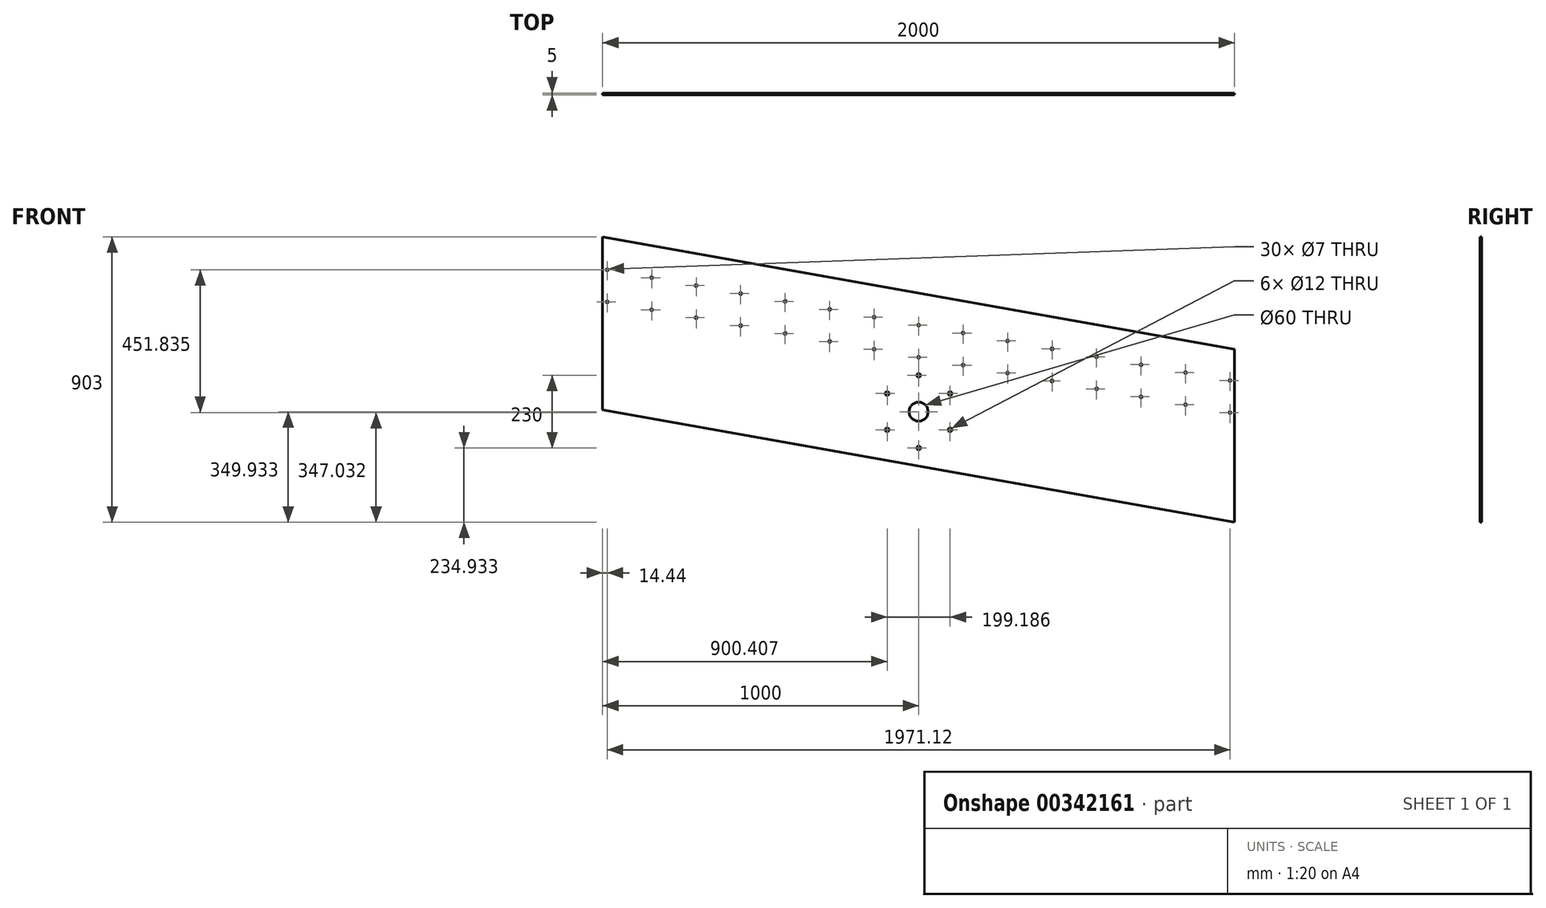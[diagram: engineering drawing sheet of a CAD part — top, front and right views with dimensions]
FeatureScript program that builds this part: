
annotation { "Feature Type Name" : "Feature", "Feature Type Description" : "" }
export const myFeature = defineFeature(function(context is Context, id is Id, definition is map)
    precondition{}
    {
        {
            var Q0;
            Q0=qCreatedBy(makeId("Front.planeOp"),FACE);
            var sketch = newSketch(context, id + "F0", { "sketchPlane" : qUnion([Q0])});
            skLineSegment(sketch, "E0", {"start": v(1435, 0) * mm, "end": v(1435, 547.6) * mm});
            skLineSegment(sketch, "E1", {"start": v(1435, 547.6) * mm, "end": v(-565, 903) * mm});
            skLineSegment(sketch, "E2", {"start": v(-565, 903) * mm, "end": v(-565, 355.4) * mm});
            skLineSegment(sketch, "E3", {"start": v(1435, 344.47) * mm, "end": v(1420.56, 347.03) * mm, "construction": true});
            skCircle(sketch, "E4", {"center": v(-550.56, 798.87) * mm, "radius": 3.5 * mm});
            skCircle(sketch, "E5", {"center": v(-550.56, 697.3) * mm, "radius": 3.5 * mm});
            skLineSegment(sketch, "E6.1.0.0", {"start": v(-409.77, 773.85) * mm, "end": v(-409.77, 672.28) * mm, "construction": true});
            skCircle(sketch, "E6.1.0.1", {"center": v(-409.77, 773.85) * mm, "radius": 3.5 * mm});
            skCircle(sketch, "E6.1.0.2", {"center": v(-409.77, 672.28) * mm, "radius": 3.5 * mm});
            skLineSegment(sketch, "E6.2.0.0", {"start": v(-268.97, 748.83) * mm, "end": v(-268.97, 647.26) * mm, "construction": true});
            skCircle(sketch, "E6.2.0.1", {"center": v(-268.97, 748.83) * mm, "radius": 3.5 * mm});
            skCircle(sketch, "E6.2.0.2", {"center": v(-268.97, 647.26) * mm, "radius": 3.5 * mm});
            skLineSegment(sketch, "E6.3.0.0", {"start": v(-128.18, 723.8) * mm, "end": v(-128.18, 622.24) * mm, "construction": true});
            skCircle(sketch, "E6.3.0.1", {"center": v(-128.18, 723.8) * mm, "radius": 3.5 * mm});
            skCircle(sketch, "E6.3.0.2", {"center": v(-128.18, 622.24) * mm, "radius": 3.5 * mm});
            skLineSegment(sketch, "E6.4.0.0", {"start": v(12.62, 698.8) * mm, "end": v(12.62, 597.22) * mm, "construction": true});
            skCircle(sketch, "E6.4.0.1", {"center": v(12.62, 698.8) * mm, "radius": 3.5 * mm});
            skCircle(sketch, "E6.4.0.2", {"center": v(12.62, 597.22) * mm, "radius": 3.5 * mm});
            skLineSegment(sketch, "E6.5.0.0", {"start": v(153.41, 673.77) * mm, "end": v(153.41, 572.2) * mm, "construction": true});
            skCircle(sketch, "E6.5.0.1", {"center": v(153.41, 673.77) * mm, "radius": 3.5 * mm});
            skCircle(sketch, "E6.5.0.2", {"center": v(153.41, 572.2) * mm, "radius": 3.5 * mm});
            skLineSegment(sketch, "E6.6.0.0", {"start": v(294.2, 648.75) * mm, "end": v(294.2, 547.19) * mm, "construction": true});
            skCircle(sketch, "E6.6.0.1", {"center": v(294.2, 648.75) * mm, "radius": 3.5 * mm});
            skCircle(sketch, "E6.6.0.2", {"center": v(294.2, 547.19) * mm, "radius": 3.5 * mm});
            skLineSegment(sketch, "E6.7.0.0", {"start": v(435, 623.73) * mm, "end": v(435, 522.17) * mm, "construction": true});
            skCircle(sketch, "E6.7.0.1", {"center": v(435, 623.73) * mm, "radius": 3.5 * mm});
            skCircle(sketch, "E6.7.0.2", {"center": v(435, 522.17) * mm, "radius": 3.5 * mm});
            skLineSegment(sketch, "E6.8.0.0", {"start": v(575.8, 598.71) * mm, "end": v(575.8, 497.15) * mm, "construction": true});
            skCircle(sketch, "E6.8.0.1", {"center": v(575.8, 598.71) * mm, "radius": 3.5 * mm});
            skCircle(sketch, "E6.8.0.2", {"center": v(575.8, 497.15) * mm, "radius": 3.5 * mm});
            skLineSegment(sketch, "E6.9.0.0", {"start": v(716.59, 573.7) * mm, "end": v(716.59, 472.13) * mm, "construction": true});
            skCircle(sketch, "E6.9.0.1", {"center": v(716.59, 573.7) * mm, "radius": 3.5 * mm});
            skCircle(sketch, "E6.9.0.2", {"center": v(716.59, 472.13) * mm, "radius": 3.5 * mm});
            skLineSegment(sketch, "E6.10.0.0", {"start": v(857.38, 548.68) * mm, "end": v(857.38, 447.1) * mm, "construction": true});
            skCircle(sketch, "E6.10.0.1", {"center": v(857.38, 548.68) * mm, "radius": 3.5 * mm});
            skCircle(sketch, "E6.10.0.2", {"center": v(857.38, 447.1) * mm, "radius": 3.5 * mm});
            skLineSegment(sketch, "E6.11.0.0", {"start": v(998.18, 523.66) * mm, "end": v(998.18, 422.09) * mm, "construction": true});
            skCircle(sketch, "E6.11.0.1", {"center": v(998.18, 523.66) * mm, "radius": 3.5 * mm});
            skCircle(sketch, "E6.11.0.2", {"center": v(998.18, 422.09) * mm, "radius": 3.5 * mm});
            skLineSegment(sketch, "E6.12.0.0", {"start": v(1138.97, 498.64) * mm, "end": v(1138.97, 397.07) * mm, "construction": true});
            skCircle(sketch, "E6.12.0.1", {"center": v(1138.97, 498.64) * mm, "radius": 3.5 * mm});
            skCircle(sketch, "E6.12.0.2", {"center": v(1138.97, 397.07) * mm, "radius": 3.5 * mm});
            skLineSegment(sketch, "E6.13.0.0", {"start": v(1279.77, 473.62) * mm, "end": v(1279.77, 372.05) * mm, "construction": true});
            skCircle(sketch, "E6.13.0.1", {"center": v(1279.77, 473.62) * mm, "radius": 3.5 * mm});
            skCircle(sketch, "E6.13.0.2", {"center": v(1279.77, 372.05) * mm, "radius": 3.5 * mm});
            skLineSegment(sketch, "E6.14.0.0", {"start": v(1420.56, 448.6) * mm, "end": v(1420.56, 347.03) * mm, "construction": true});
            skCircle(sketch, "E6.14.0.1", {"center": v(1420.56, 448.6) * mm, "radius": 3.5 * mm});
            skCircle(sketch, "E6.14.0.2", {"center": v(1420.56, 347.03) * mm, "radius": 3.5 * mm});
            skLineSegment(sketch, "E6.direction1", {"start": v(-550.56, 697.3) * mm, "end": v(-409.77, 672.28) * mm, "construction": true});
            skLineSegment(sketch, "E7", {"start": v(1420.56, 347.03) * mm, "end": v(-550.56, 697.3) * mm, "construction": true});
            skLineSegment(sketch, "E8", {"start": v(1420.56, 448.6) * mm, "end": v(1435, 446.03) * mm, "construction": true});
            skLineSegment(sketch, "E9", {"start": v(-550.56, 697.3) * mm, "end": v(-565, 699.87) * mm, "construction": true});
            skLineSegment(sketch, "E10", {"start": v(-550.56, 798.87) * mm, "end": v(-550.56, 697.3) * mm, "construction": true});
            skLineSegment(sketch, "E11", {"start": v(-550.56, 798.87) * mm, "end": v(1420.56, 448.6) * mm, "construction": true});
            skLineSegment(sketch, "E12", {"start": v(-550.56, 798.87) * mm, "end": v(-565, 801.43) * mm, "construction": true});
            skLineSegment(sketch, "E13", {"start": v(0, 0) * mm, "end": v(1435, 0) * mm, "construction": true});
            skLineSegment(sketch, "E14", {"start": v(0, 0) * mm, "end": v(0, 255) * mm, "construction": true});
            skLineSegment(sketch, "E15", {"start": v(0, 255) * mm, "end": v(1435, 0) * mm, "construction": true});
            skLineSegment(sketch, "E16", {"start": v(0, 255) * mm, "end": v(-565, 355.4) * mm});
            skLineSegment(sketch, "E17", {"start": v(0, 255) * mm, "end": v(1435, 0) * mm});
            skLineSegment(sketch, "E18", {"start": v(435, 522.17) * mm, "end": v(435, 177.7) * mm, "construction": true});
            skLineSegment(sketch, "E19", {"start": v(435, 349.93) * mm, "end": v(285, 349.93) * mm, "construction": true});
            skPoint(sketch, "E19.endSnap0", {"position": v(435, 349.93) * mm});
            skLineSegment(sketch, "E20", {"start": v(435, 349.93) * mm, "end": v(585, 349.93) * mm, "construction": true});
            skCircle(sketch, "E21", {"center": v(435, 349.93) * mm, "radius": 115 * mm, "construction": true});
            skCircle(sketch, "E22", {"center": v(435, 464.93) * mm, "radius": 6 * mm});
            skCircle(sketch, "E23.1.0", {"center": v(335.4, 407.43) * mm, "radius": 6 * mm});
            skCircle(sketch, "E23.2.0", {"center": v(335.4, 292.43) * mm, "radius": 6 * mm});
            skCircle(sketch, "E23.3.0", {"center": v(435, 234.93) * mm, "radius": 6 * mm});
            skCircle(sketch, "E23.4.0", {"center": v(534.6, 292.43) * mm, "radius": 6 * mm});
            skCircle(sketch, "E23.5.0", {"center": v(534.6, 407.43) * mm, "radius": 6 * mm});
            skCircle(sketch, "E24", {"center": v(435, 349.93) * mm, "radius": 30 * mm});
            skSolve(sketch);
        }
        {
            var Q0;
            Q0=qSketchRegion(id+"F0",true);
            var Q1;
            Q1=makeQuery(id+"F0.imprint","IMPRINT",FACE,{"disambiguationData":[TD([[makeQuery(id+"F0.imprint","IMPRINT",EDGE,{"derivedFrom":sQuery(id+"F0.wireOp",EDGE,"jSg4FRcu-u39U-EJTX-ydAV-j8xegxBfcqbr")}),1.0]])]});
            extrude(context, id + "F1", {"entities" : qUnion([Q0, Q1]), "endBound" : BoundingType.SYMMETRIC, "depth" : 5 * mm});
        }
    });
